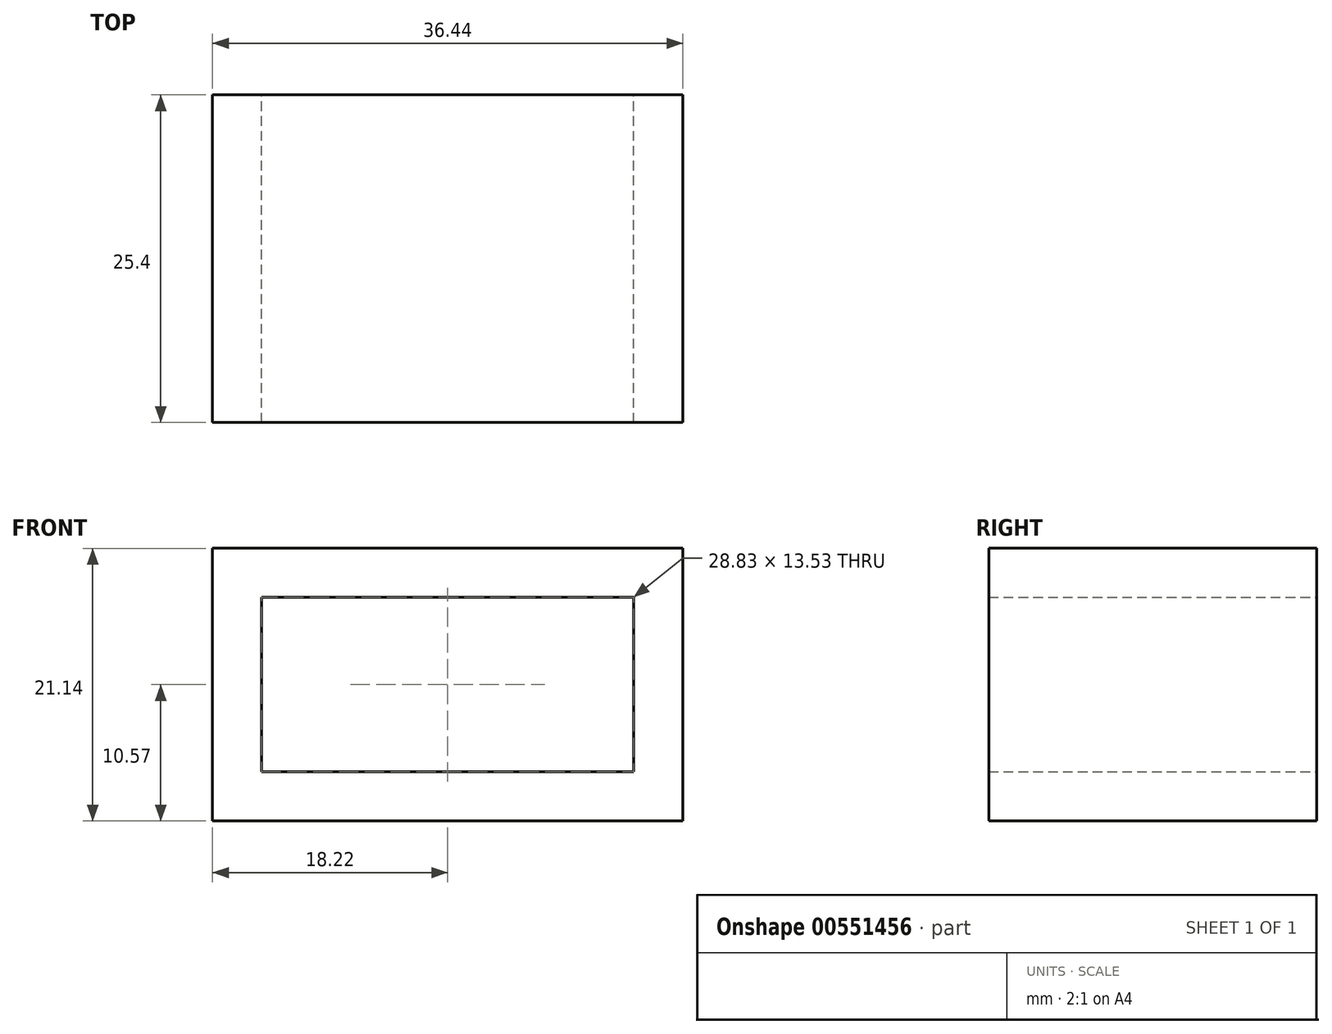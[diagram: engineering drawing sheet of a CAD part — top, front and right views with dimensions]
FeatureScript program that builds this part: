
annotation { "Feature Type Name" : "Feature", "Feature Type Description" : "" }
export const myFeature = defineFeature(function(context is Context, id is Id, definition is map)
    precondition{}
    {
        {
            var Q0;
            Q0=qCreatedBy(makeId("Front.planeOp"),FACE);
            var sketch = newSketch(context, id + "F0", { "sketchPlane" : qUnion([Q0])});
            skLineSegment(sketch, "E0.bottom", {"start": v(14.41, 6.76) * mm, "end": v(-14.41, 6.76) * mm});
            skLineSegment(sketch, "E0.top", {"start": v(14.41, -6.76) * mm, "end": v(-14.41, -6.76) * mm});
            skLineSegment(sketch, "E0.left", {"start": v(14.41, 6.76) * mm, "end": v(14.41, -6.76) * mm});
            skLineSegment(sketch, "E0.right", {"start": v(-14.41, 6.76) * mm, "end": v(-14.41, -6.76) * mm});
            skPoint(sketch, "E0.middle", {"position": v(0, 0) * mm});
            skLineSegment(sketch, "E1.bottom", {"start": v(18.22, 10.57) * mm, "end": v(-18.22, 10.57) * mm});
            skLineSegment(sketch, "E1.top", {"start": v(18.22, -10.57) * mm, "end": v(-18.22, -10.57) * mm});
            skLineSegment(sketch, "E1.left", {"start": v(18.22, 10.57) * mm, "end": v(18.22, -10.57) * mm});
            skLineSegment(sketch, "E1.right", {"start": v(-18.22, 10.57) * mm, "end": v(-18.22, -10.57) * mm});
            skSolve(sketch);
        }
        {
            var Q0;
            Q0 = qSketchRegion(id + "F0", true);
            extrude(context, id + "F1", {"entities" : qUnion([Q0]), "depth" : 25.4 * mm, "offsetDistance" : 25.4 * mm});
        }
    });
